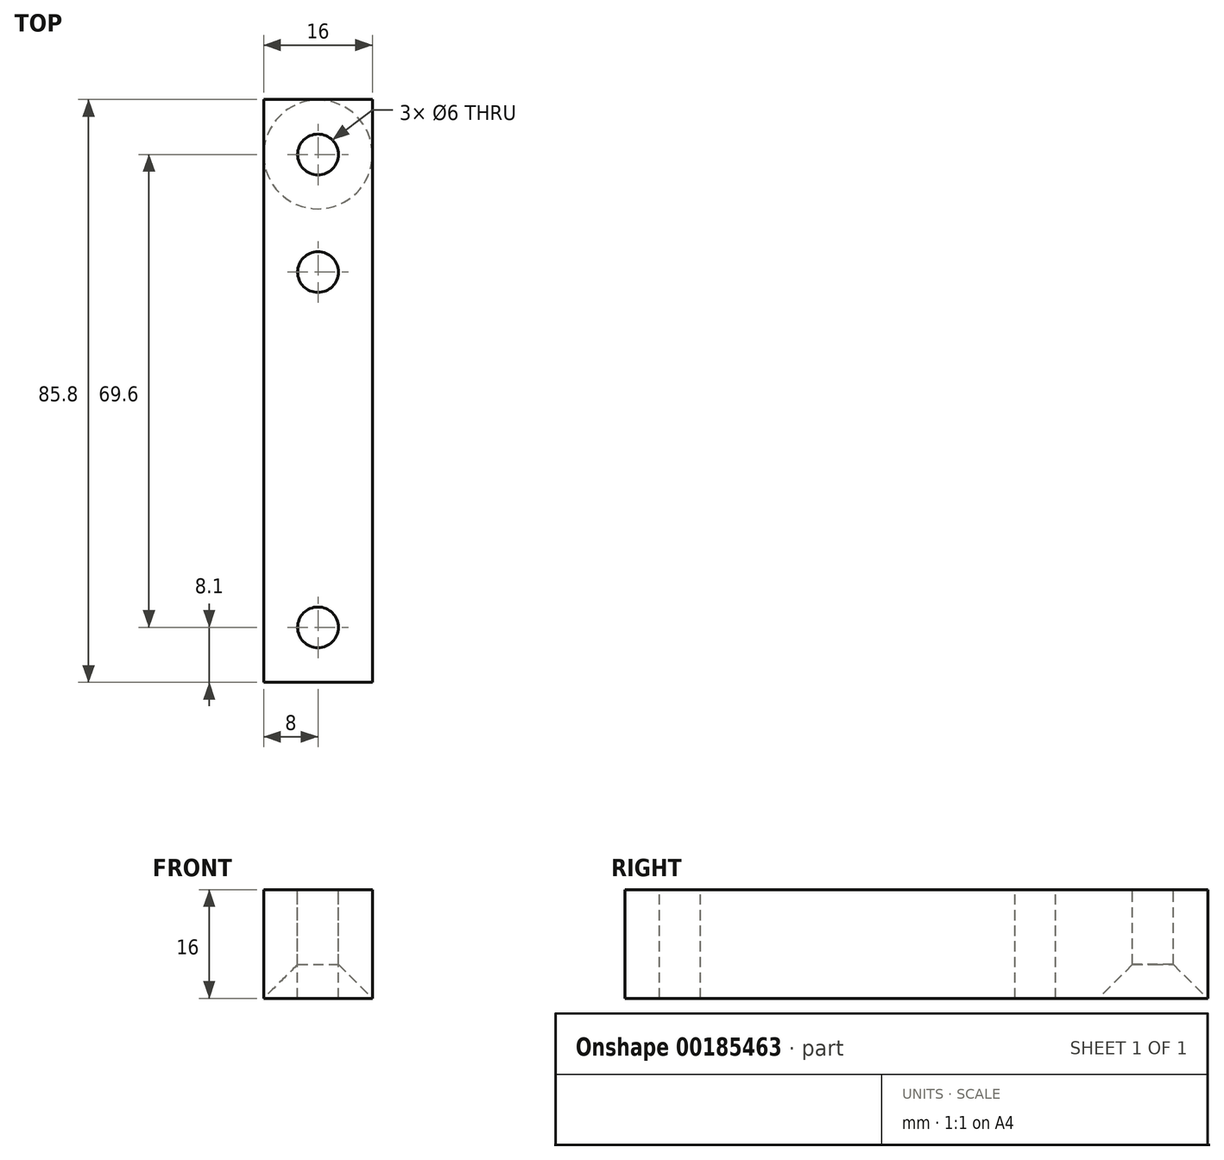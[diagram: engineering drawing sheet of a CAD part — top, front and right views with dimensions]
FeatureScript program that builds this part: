
annotation { "Feature Type Name" : "Feature", "Feature Type Description" : "" }
export const myFeature = defineFeature(function(context is Context, id is Id, definition is map)
    precondition{}
    {
        {
            var Q0;
            Q0=qCreatedBy(makeId("Front.planeOp"),FACE);
            var sketch = newSketch(context, id + "F5", { "sketchPlane" : qUnion([Q0])});
            skLineSegment(sketch, "E0.bottom", {"start": v(8, 8) * mm, "end": v(-8, 8) * mm});
            skLineSegment(sketch, "E0.top", {"start": v(8, -8) * mm, "end": v(-8, -8) * mm});
            skLineSegment(sketch, "E0.left", {"start": v(8, 8) * mm, "end": v(8, -8) * mm});
            skLineSegment(sketch, "E0.right", {"start": v(-8, 8) * mm, "end": v(-8, -8) * mm});
            skPoint(sketch, "E0.middle", {"position": v(0, 0) * mm});
            skSolve(sketch);
        }
        {
            var Q0;
            Q0=makeQuery(id+"F5.imprint","IMPRINT",FACE,{"disambiguationData":[TD([[makeQuery(id+"F5.imprint","IMPRINT",EDGE,{"derivedFrom":sQuery(id+"F5.wireOp",EDGE,"E0.bottom")}),1.0]])]});
            extrude(context, id + "F6", {"entities" : qUnion([Q0]), "endBound" : BoundingType.SYMMETRIC, "depth" : 85.8 * mm});
        }
        {
            var Q0;
            Q0=qCreatedBy(makeId("Top.planeOp"),FACE);
            var sketch = newSketch(context, id + "F0", { "sketchPlane" : qUnion([Q0])});
            skCircle(sketch, "E1", {"center": v(0, -34.8) * mm, "radius": 3 * mm});
            skCircle(sketch, "E2", {"center": v(0, 34.8) * mm, "radius": 3 * mm});
            skSolve(sketch);
        }
        {
            var Q0;
            Q0 = qSketchRegion(id + "F0", true);
            extrude(context, id + "F7", {"entities" : qUnion([Q0]), "operationType" : NewBodyOperationType.REMOVE, "endBound" : BoundingType.SYMMETRIC, "oppositeDirection" : true, "depth" : 25 * mm});
        }
        {
            var Q0;
            Q0=makeQuery(id+"F6.opExtrude","SWEPT_FACE",FACE,{"disambiguationData":[OSD([sQuery(id+"F5.wireOp",EDGE,"E0.bottom")])]});
            var sketch = newSketch(context, id + "F1", { "sketchPlane" : qUnion([Q0])});
            skCircle(sketch, "E3", {"center": v(34.8, 0) * mm, "radius": 36.5 * mm});
            skSolve(sketch);
        }
        {
            var Q0;
            Q0=makeQuery(id+"F6.opExtrude","SWEPT_FACE",FACE,{"disambiguationData":[OSD([sQuery(id+"F5.wireOp",EDGE,"E0.bottom")])]});
            var sketch = newSketch(context, id + "F8", { "sketchPlane" : qUnion([Q0])});
            skLineSegment(sketch, "E4.bottom", {"start": v(8, 24.78) * mm, "end": v(-8, 24.78) * mm});
            skLineSegment(sketch, "E4.top", {"start": v(8, -24.78) * mm, "end": v(-8, -24.78) * mm});
            skLineSegment(sketch, "E4.left", {"start": v(8, 24.78) * mm, "end": v(8, -24.78) * mm});
            skLineSegment(sketch, "E4.right", {"start": v(-8, 24.78) * mm, "end": v(-8, -24.78) * mm});
            skSolve(sketch);
        }
        {
            var Q0;
            Q0=makeQuery(id+"F7.boolean.opBoolean","INTERSECT",EDGE,{"derivedFrom":[makeQuery(id+"F6.opExtrude","SWEPT_FACE",FACE,{"disambiguationData":[OSD([sQuery(id+"F5.wireOp",EDGE,"E0.top")])]}),makeQuery(id+"F7.opExtrude","SWEPT_FACE",FACE,{"disambiguationData":[OSD([sQuery(id+"F0.wireOp",EDGE,"E2")])]})]});
            chamfer(context, id + "F2", {"entities" : qUnion([Q0]), "width" : 5 * mm, "tangentPropagation" : true});
        }
        {
            var Q0;
            Q0=makeQuery(id+"F6.opExtrude","SWEPT_FACE",FACE,{"disambiguationData":[OSD([sQuery(id+"F5.wireOp",EDGE,"E0.bottom")])]});
            var sketch = newSketch(context, id + "F3", { "sketchPlane" : qUnion([Q0])});
            skCircle(sketch, "E5", {"center": v(0, 17.5) * mm, "radius": 3 * mm});
            skSolve(sketch);
        }
        {
            var Q0;
            Q0=makeQuery(id+"F3.imprint","IMPRINT",FACE,{"disambiguationData":[TD([[makeQuery(id+"F3.imprint","IMPRINT",EDGE,{"derivedFrom":sQuery(id+"F3.wireOp",EDGE,"E5")}),1.0]])]});
            extrude(context, id + "F4", {"entities" : qUnion([Q0]), "operationType" : NewBodyOperationType.REMOVE, "endBound" : BoundingType.THROUGH_ALL, "oppositeDirection" : true, "depth" : 25 * mm});
        }
    });
